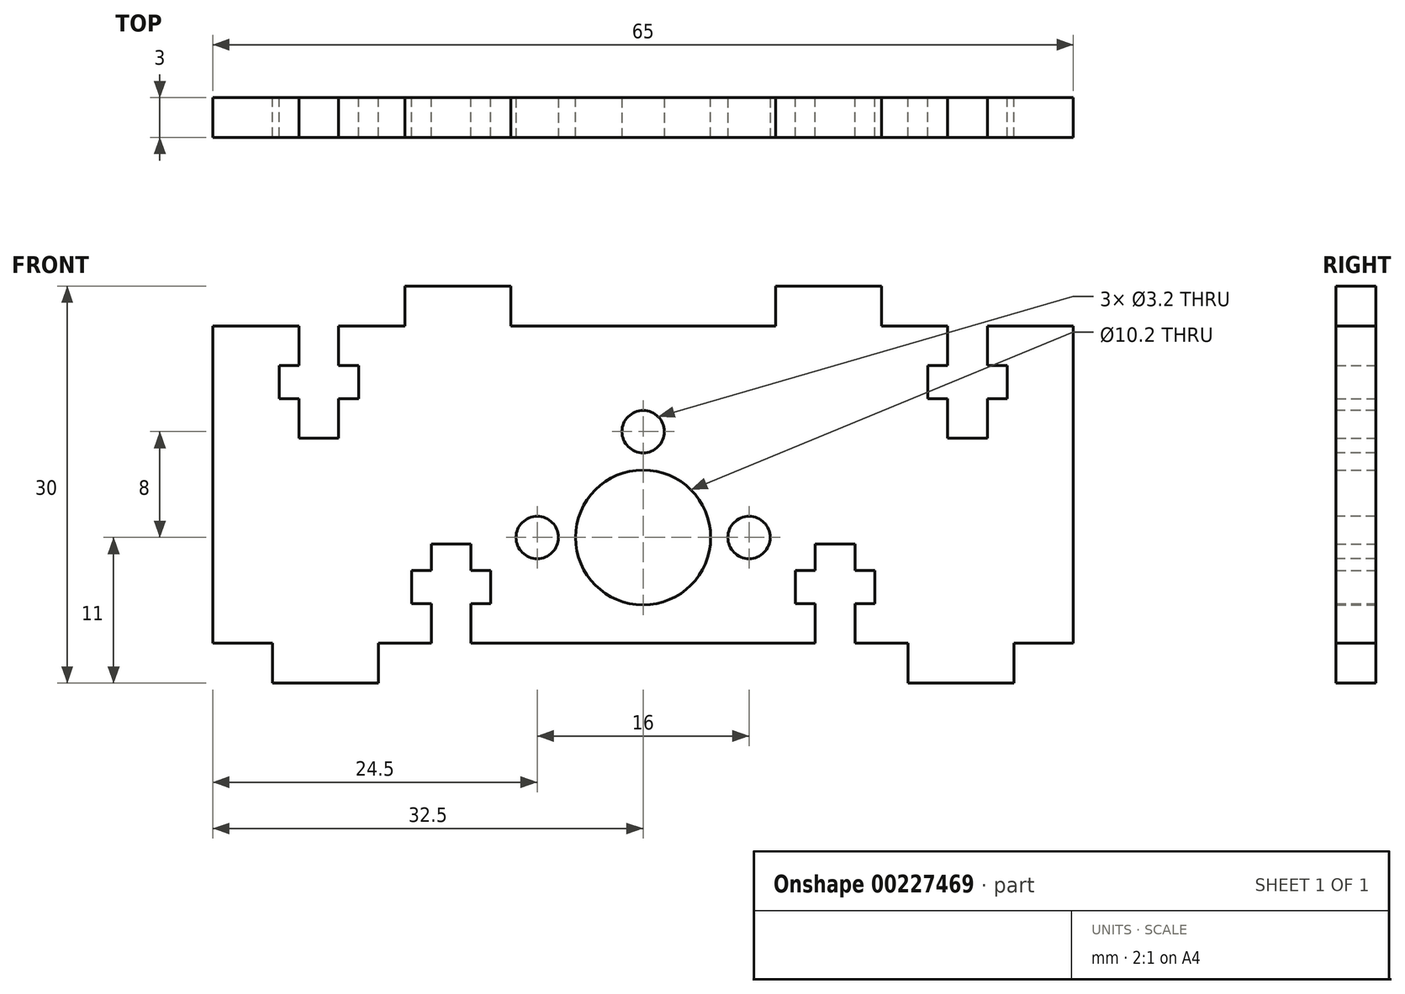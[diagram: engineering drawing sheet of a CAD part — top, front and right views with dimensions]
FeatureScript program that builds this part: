
annotation { "Feature Type Name" : "Feature", "Feature Type Description" : "" }
export const myFeature = defineFeature(function(context is Context, id is Id, definition is map)
    precondition{}
    {
        {
            var Q0;
            Q0=qCreatedBy(makeId("Front.planeOp"),FACE);
            var sketch = newSketch(context, id + "F0", { "sketchPlane" : qUnion([Q0])});
            skLineSegment(sketch, "E0.left", {"start": v(32.5, -8) * mm, "end": v(32.5, 16) * mm});
            skLineSegment(sketch, "E0.right", {"start": v(-32.5, -8) * mm, "end": v(-32.5, 16) * mm});
            skPoint(sketch, "E0.middle", {"position": v(0, 0) * mm});
            skCircle(sketch, "E1", {"center": v(0, 0) * mm, "radius": 5.1 * mm});
            skPoint(sketch, "E2", {"position": v(0, -8) * mm});
            skLineSegment(sketch, "E3", {"start": v(0, -8) * mm, "end": v(20, -8) * mm});
            skLineSegment(sketch, "E4", {"start": v(20, -8) * mm, "end": v(20, -11) * mm});
            skLineSegment(sketch, "E5", {"start": v(20, -11) * mm, "end": v(28, -11) * mm});
            skLineSegment(sketch, "E6", {"start": v(28, -11) * mm, "end": v(28, -8) * mm});
            skLineSegment(sketch, "E7.MirrorCS", {"start": v(0, -8) * mm, "end": v(-20, -8) * mm});
            skLineSegment(sketch, "E8.MirrorCS", {"start": v(-20, -8) * mm, "end": v(-20, -11) * mm});
            skLineSegment(sketch, "E9.MirrorCS", {"start": v(-20, -11) * mm, "end": v(-28, -11) * mm});
            skLineSegment(sketch, "E10.MirrorCS", {"start": v(-28, -11) * mm, "end": v(-28, -8) * mm});
            skLineSegment(sketch, "E11", {"start": v(32.5, -8) * mm, "end": v(28, -8) * mm});
            skLineSegment(sketch, "E12", {"start": v(-28, -8) * mm, "end": v(-32.5, -8) * mm});
            skPoint(sketch, "E13", {"position": v(0, 16) * mm});
            skLineSegment(sketch, "E14", {"start": v(-32.5, 16) * mm, "end": v(-18, 16) * mm});
            skLineSegment(sketch, "E15", {"start": v(-18, 16) * mm, "end": v(-18, 19) * mm});
            skLineSegment(sketch, "E16", {"start": v(-18, 19) * mm, "end": v(-10, 19) * mm});
            skLineSegment(sketch, "E17", {"start": v(-10, 19) * mm, "end": v(-10, 16) * mm});
            skLineSegment(sketch, "E18", {"start": v(-10, 16) * mm, "end": v(0, 16) * mm});
            skLineSegment(sketch, "E19.MirrorCS", {"start": v(10, 16) * mm, "end": v(0, 16) * mm});
            skLineSegment(sketch, "E20.MirrorCS", {"start": v(10, 19) * mm, "end": v(10, 16) * mm});
            skLineSegment(sketch, "E21.MirrorCS", {"start": v(18, 19) * mm, "end": v(10, 19) * mm});
            skLineSegment(sketch, "E22.MirrorCS", {"start": v(18, 16) * mm, "end": v(18, 19) * mm});
            skLineSegment(sketch, "E23.MirrorCS", {"start": v(32.5, 16) * mm, "end": v(18, 16) * mm});
            skSolve(sketch);
        }
        {
            var Q0;
            Q0=makeQuery(id+"F0.imprint","IMPRINT",FACE,{"disambiguationData":[TD([[makeQuery(id+"F0.imprint","IMPRINT",EDGE,{"derivedFrom":sQuery(id+"F0.wireOp",EDGE,"E0.left")}),1.0]])]});
            extrude(context, id + "F1", {"entities" : qUnion([Q0]), "depth" : 3 * mm});
        }
        {
            var Q0;
            Q0=makeQuery(id+"F1.opExtrude","CAP_FACE",FACE,{"disambiguationData":[OSD([sQuery(id+"F0.wireOp",EDGE,"E0.top"),sQuery(id+"F0.wireOp",EDGE,"E0.left"),sQuery(id+"F0.wireOp",EDGE,"E0.right"),sQuery(id+"F0.wireOp",EDGE,"E1"),sQuery(id+"F0.wireOp",EDGE,"E3"),sQuery(id+"F0.wireOp",EDGE,"E4"),sQuery(id+"F0.wireOp",EDGE,"E5"),sQuery(id+"F0.wireOp",EDGE,"E6"),sQuery(id+"F0.wireOp",EDGE,"Bye9wKvp-iTN6-aMiy-t3HV-321I6idTwAT7"),sQuery(id+"F0.wireOp",EDGE,"MaIOWbBU-8FJR-umEs-W0u1-0UBdhOL1jX3R"),sQuery(id+"F0.wireOp",EDGE,"cjjMekjN-d9GH-w392-u9fJ-7fXVraFaPUEF"),sQuery(id+"F0.wireOp",EDGE,"r4o5ajzM-Rsn6-LwNu-8ZH8-RrZPdrBqQNhf"),sQuery(id+"F0.wireOp",EDGE,"4rBLy9Cv-BTZd-DXYO-WPMD-THVSlvj0M45P"),sQuery(id+"F0.wireOp",EDGE,"0QHm3L1z-PB8E-sUM8-9Iu7-9ylB9Zyak7ZM"),sQuery(id+"F0.wireOp",EDGE,"lGSHjSAP-HDtq-xCeI-DjX7-dJADT3ItqI3i"),sQuery(id+"F0.wireOp",EDGE,"hqEljnGM-RK9Z-ywhK-KnxT-DgdnVdAw69hx"),sQuery(id+"F0.wireOp",EDGE,"3JF1scFz-tUfL-0J2I-GCU2-pg9Iem59yael"),sQuery(id+"F0.wireOp",EDGE,"VIemKg7s-0Qql-9ATH-uaDb-s28MwwDJACN2"),sQuery(id+"F0.wireOp",EDGE,"SrsuBa1K-ROI0-YVy5-osGe-RaKEGjTI8dTk"),sQuery(id+"F0.wireOp",EDGE,"fkxjX4On-I71C-g2Ab-9X9a-8QQVlJaSbmEA"),sQuery(id+"F0.wireOp",EDGE,"fKuv9ndE-aQbh-sH4q-A6gn-ncGJMZsXg4NX"),sQuery(id+"F0.wireOp",EDGE,"E7.MirrorCS"),sQuery(id+"F0.wireOp",EDGE,"E8.MirrorCS"),sQuery(id+"F0.wireOp",EDGE,"E9.MirrorCS"),sQuery(id+"F0.wireOp",EDGE,"E10.MirrorCS"),sQuery(id+"F0.wireOp",EDGE,"167239a6-6452-41fe-82d5-06518cd1e7ca0.MirrorCS"),sQuery(id+"F0.wireOp",EDGE,"4d03efd5-a7b2-448c-9269-3b157b8b6a3f0.MirrorCS"),sQuery(id+"F0.wireOp",EDGE,"4a9de9e8-4b7a-41f9-be51-9981378ba4400.MirrorCS"),sQuery(id+"F0.wireOp",EDGE,"477fae85-c943-47b6-9154-c00c6ce072b60.MirrorCS"),sQuery(id+"F0.wireOp",EDGE,"f8cb59b5-f55e-4440-885b-3b89e86697820.MirrorCS"),sQuery(id+"F0.wireOp",EDGE,"5bb5084e-da35-4d76-b03d-406c150248a20.MirrorCS"),sQuery(id+"F0.wireOp",EDGE,"8fed15e2-98f6-4966-a165-82ee8002b8fb0.MirrorCS"),sQuery(id+"F0.wireOp",EDGE,"7ee60ff3-4344-4ca1-8754-2f7ee897794d0.MirrorCS"),sQuery(id+"F0.wireOp",EDGE,"6a09c46f-801d-4278-9024-28b163129c370.MirrorCS"),sQuery(id+"F0.wireOp",EDGE,"90cf5c0c-33e3-46b7-a68c-16b02a4c827a0.MirrorCS"),sQuery(id+"F0.wireOp",EDGE,"6cdd3639-f48b-44bc-9e45-be0ea5840fc20.MirrorCS"),sQuery(id+"F0.wireOp",EDGE,"234d0976-2521-4b2c-bc8e-cd19e18f5db30.MirrorCS"),sQuery(id+"F0.wireOp",EDGE,"0711aa81-e21d-44fe-b418-f76be042628f0.MirrorCS")])],"isStart":true});
            var sketch = newSketch(context, id + "F2", { "sketchPlane" : qUnion([Q0])});
            skLineSegment(sketch, "E24", {"start": v(13, -8) * mm, "end": v(13, -5) * mm});
            skLineSegment(sketch, "E25", {"start": v(13, -5) * mm, "end": v(11.5, -5) * mm});
            skLineSegment(sketch, "E26", {"start": v(11.5, -5) * mm, "end": v(11.5, -2.5) * mm});
            skLineSegment(sketch, "E27", {"start": v(11.5, -2.5) * mm, "end": v(13, -2.5) * mm});
            skLineSegment(sketch, "E28", {"start": v(13, -2.5) * mm, "end": v(13, -0.5) * mm});
            skLineSegment(sketch, "E29", {"start": v(13, -0.5) * mm, "end": v(16, -0.5) * mm});
            skLineSegment(sketch, "E30", {"start": v(16, -0.5) * mm, "end": v(16, -2.5) * mm});
            skLineSegment(sketch, "E31", {"start": v(16, -2.5) * mm, "end": v(17.5, -2.5) * mm});
            skLineSegment(sketch, "E32", {"start": v(17.5, -2.5) * mm, "end": v(17.5, -5) * mm});
            skLineSegment(sketch, "E33", {"start": v(17.5, -5) * mm, "end": v(16, -5) * mm});
            skLineSegment(sketch, "E34", {"start": v(16, -5) * mm, "end": v(16, -8) * mm});
            skPoint(sketch, "E35", {"position": v(14.5, -8) * mm});
            skLineSegment(sketch, "E36", {"start": v(16, -8) * mm, "end": v(13, -8) * mm});
            skLineSegment(sketch, "E37.MirrorCS", {"start": v(-13, -2.5) * mm, "end": v(-13, -0.5) * mm});
            skLineSegment(sketch, "E38.MirrorCS", {"start": v(-13, -5) * mm, "end": v(-11.5, -5) * mm});
            skLineSegment(sketch, "E39.MirrorCS", {"start": v(-11.5, -5) * mm, "end": v(-11.5, -2.5) * mm});
            skLineSegment(sketch, "E40.MirrorCS", {"start": v(-16, -0.5) * mm, "end": v(-16, -2.5) * mm});
            skLineSegment(sketch, "E41.MirrorCS", {"start": v(-17.5, -5) * mm, "end": v(-16, -5) * mm});
            skLineSegment(sketch, "E42.MirrorCS", {"start": v(-11.5, -2.5) * mm, "end": v(-13, -2.5) * mm});
            skLineSegment(sketch, "E43.MirrorCS", {"start": v(-17.5, -2.5) * mm, "end": v(-17.5, -5) * mm});
            skLineSegment(sketch, "E44.MirrorCS", {"start": v(-16, -2.5) * mm, "end": v(-17.5, -2.5) * mm});
            skLineSegment(sketch, "E45.MirrorCS", {"start": v(-16, -8) * mm, "end": v(-13, -8) * mm});
            skLineSegment(sketch, "E46.MirrorCS", {"start": v(-13, -0.5) * mm, "end": v(-16, -0.5) * mm});
            skLineSegment(sketch, "E47.MirrorCS", {"start": v(-13, -8) * mm, "end": v(-13, -5) * mm});
            skPoint(sketch, "E48.MirrorP", {"position": v(-14.5, -8) * mm});
            skLineSegment(sketch, "E49.MirrorCS", {"start": v(-16, -5) * mm, "end": v(-16, -8) * mm});
            skLineSegment(sketch, "E50", {"start": v(26, 16) * mm, "end": v(26, 13) * mm});
            skLineSegment(sketch, "E51", {"start": v(26, 13) * mm, "end": v(27.5, 13) * mm});
            skLineSegment(sketch, "E52", {"start": v(27.5, 13) * mm, "end": v(27.5, 10.5) * mm});
            skLineSegment(sketch, "E53", {"start": v(27.5, 10.5) * mm, "end": v(26, 10.5) * mm});
            skLineSegment(sketch, "E54", {"start": v(26, 10.5) * mm, "end": v(26, 7.5) * mm});
            skLineSegment(sketch, "E55", {"start": v(26, 7.5) * mm, "end": v(23, 7.5) * mm});
            skLineSegment(sketch, "E56", {"start": v(23, 7.5) * mm, "end": v(23, 10.5) * mm});
            skLineSegment(sketch, "E57", {"start": v(23, 10.5) * mm, "end": v(21.5, 10.5) * mm});
            skLineSegment(sketch, "E58", {"start": v(21.5, 10.5) * mm, "end": v(21.5, 13) * mm});
            skLineSegment(sketch, "E59", {"start": v(21.5, 13) * mm, "end": v(23, 13) * mm});
            skLineSegment(sketch, "E60", {"start": v(23, 13) * mm, "end": v(23, 16) * mm});
            skLineSegment(sketch, "E61", {"start": v(23, 16) * mm, "end": v(26, 16) * mm});
            skPoint(sketch, "E62", {"position": v(24.5, 16) * mm});
            skLineSegment(sketch, "E63.MirrorCS", {"start": v(-21.5, 10.5) * mm, "end": v(-21.5, 13) * mm});
            skLineSegment(sketch, "E64.MirrorCS", {"start": v(-23, 16) * mm, "end": v(-26, 16) * mm});
            skLineSegment(sketch, "E65.MirrorCS", {"start": v(-26, 7.5) * mm, "end": v(-23, 7.5) * mm});
            skPoint(sketch, "E66.MirrorP", {"position": v(-24.5, 16) * mm});
            skLineSegment(sketch, "E67.MirrorCS", {"start": v(-21.5, 13) * mm, "end": v(-23, 13) * mm});
            skLineSegment(sketch, "E68.MirrorCS", {"start": v(-23, 7.5) * mm, "end": v(-23, 10.5) * mm});
            skLineSegment(sketch, "E69.MirrorCS", {"start": v(-23, 13) * mm, "end": v(-23, 16) * mm});
            skLineSegment(sketch, "E70.MirrorCS", {"start": v(-23, 10.5) * mm, "end": v(-21.5, 10.5) * mm});
            skLineSegment(sketch, "E71.MirrorCS", {"start": v(-26, 10.5) * mm, "end": v(-26, 7.5) * mm});
            skLineSegment(sketch, "E72.MirrorCS", {"start": v(-26, 16) * mm, "end": v(-26, 13) * mm});
            skLineSegment(sketch, "E73.MirrorCS", {"start": v(-27.5, 13) * mm, "end": v(-27.5, 10.5) * mm});
            skLineSegment(sketch, "E74.MirrorCS", {"start": v(-27.5, 10.5) * mm, "end": v(-26, 10.5) * mm});
            skLineSegment(sketch, "E75.MirrorCS", {"start": v(-26, 13) * mm, "end": v(-27.5, 13) * mm});
            skSolve(sketch);
        }
        {
            var Q0;
            Q0=makeQuery(id+"F2.imprint","IMPRINT",FACE,{"disambiguationData":[TD([[makeQuery(id+"F2.imprint","IMPRINT",EDGE,{"derivedFrom":sQuery(id+"F2.wireOp",EDGE,"E24")}),-1.0]])]});
            var Q1;
            Q1=makeQuery(id+"F2.imprint","IMPRINT",FACE,{"disambiguationData":[TD([[makeQuery(id+"F2.imprint","IMPRINT",EDGE,{"derivedFrom":sQuery(id+"F2.wireOp",EDGE,"E37.MirrorCS")}),1.0]])]});
            var Q2;
            Q2=makeQuery(id+"F2.imprint","IMPRINT",FACE,{"disambiguationData":[TD([[makeQuery(id+"F2.imprint","IMPRINT",EDGE,{"derivedFrom":sQuery(id+"F2.wireOp",EDGE,"E50")}),-1.0]])]});
            var Q3;
            Q3=makeQuery(id+"F2.imprint","IMPRINT",FACE,{"disambiguationData":[TD([[makeQuery(id+"F2.imprint","IMPRINT",EDGE,{"derivedFrom":sQuery(id+"F2.wireOp",EDGE,"E63.MirrorCS")}),1.0]])]});
            extrude(context, id + "F3", {"entities" : qUnion([Q0, Q1, Q2, Q3]), "operationType" : NewBodyOperationType.REMOVE, "endBound" : BoundingType.UP_TO_NEXT, "oppositeDirection" : true, "depth" : 25 * mm});
        }
        {
            var Q0;
            Q0=makeQuery(id+"F1.opExtrude","CAP_FACE",FACE,{"disambiguationData":[OSD([sQuery(id+"F0.wireOp",EDGE,"E0.bottom"),sQuery(id+"F0.wireOp",EDGE,"E0.top"),sQuery(id+"F0.wireOp",EDGE,"E0.left"),sQuery(id+"F0.wireOp",EDGE,"E0.right"),sQuery(id+"F0.wireOp",EDGE,"E1")])],"isStart":false});
            var sketch = newSketch(context, id + "F4", { "sketchPlane" : qUnion([Q0])});
            skCircle(sketch, "E76", {"center": v(0, 0) * mm, "radius": 8 * mm, "construction": true});
            skPoint(sketch, "E77", {"position": v(0, 8) * mm});
            skPoint(sketch, "E78.1.0", {"position": v(-8, 0) * mm});
            skPoint(sketch, "E78.2.0", {"position": v(0, -8) * mm});
            skPoint(sketch, "E79.0.3.0", {"position": v(8, 0) * mm});
            skSolve(sketch);
        }
        {
            var Q0;
            Q0=sQuery(id+"F4.wireOp",VERTEX,"E78.1.0");
            var Q1;
            Q1=sQuery(id+"F4.wireOp",VERTEX,"E77");
            var Q2;
            Q2=sQuery(id+"F4.wireOp",VERTEX,"E79.0.3.0");
            var Q3;
            Q3=makeQuery(id+"F1.opExtrude","SWEPT_BODY",BODY,{"disambiguationData":[OSD([sQuery(id+"F0.wireOp",EDGE,"E0.bottom"),sQuery(id+"F0.wireOp",EDGE,"E0.top"),sQuery(id+"F0.wireOp",EDGE,"E0.left"),sQuery(id+"F0.wireOp",EDGE,"E0.right"),sQuery(id+"F0.wireOp",EDGE,"E1")])]});
            hole(context, id + "F5", {"style" : HoleStyle.SIMPLE, "endStyle" : HoleEndStyle.BLIND, "standardTappedOrClearance" : lookupTablePath({ "standard" : "ISO", "engagement" : "75%", "pitch" : "0.75 mm", "size" : "M4", "type" : "Tapped" }), "standardBlindInLast" : lookupTablePath({ "standard" : "ISO", "engagement" : "75%", "pitch" : "0.75 mm", "size" : "M4", "type" : "Tapped" }), "holeDiameter" : 3.2 * mm, "holeDepth" : 10 * mm, "locations" : qUnion([Q0, Q1, Q2]), "scope" : qUnion([Q3]), "tappedDepth" : 12 * mm, "tapClearance" : 3});
        }
    });
